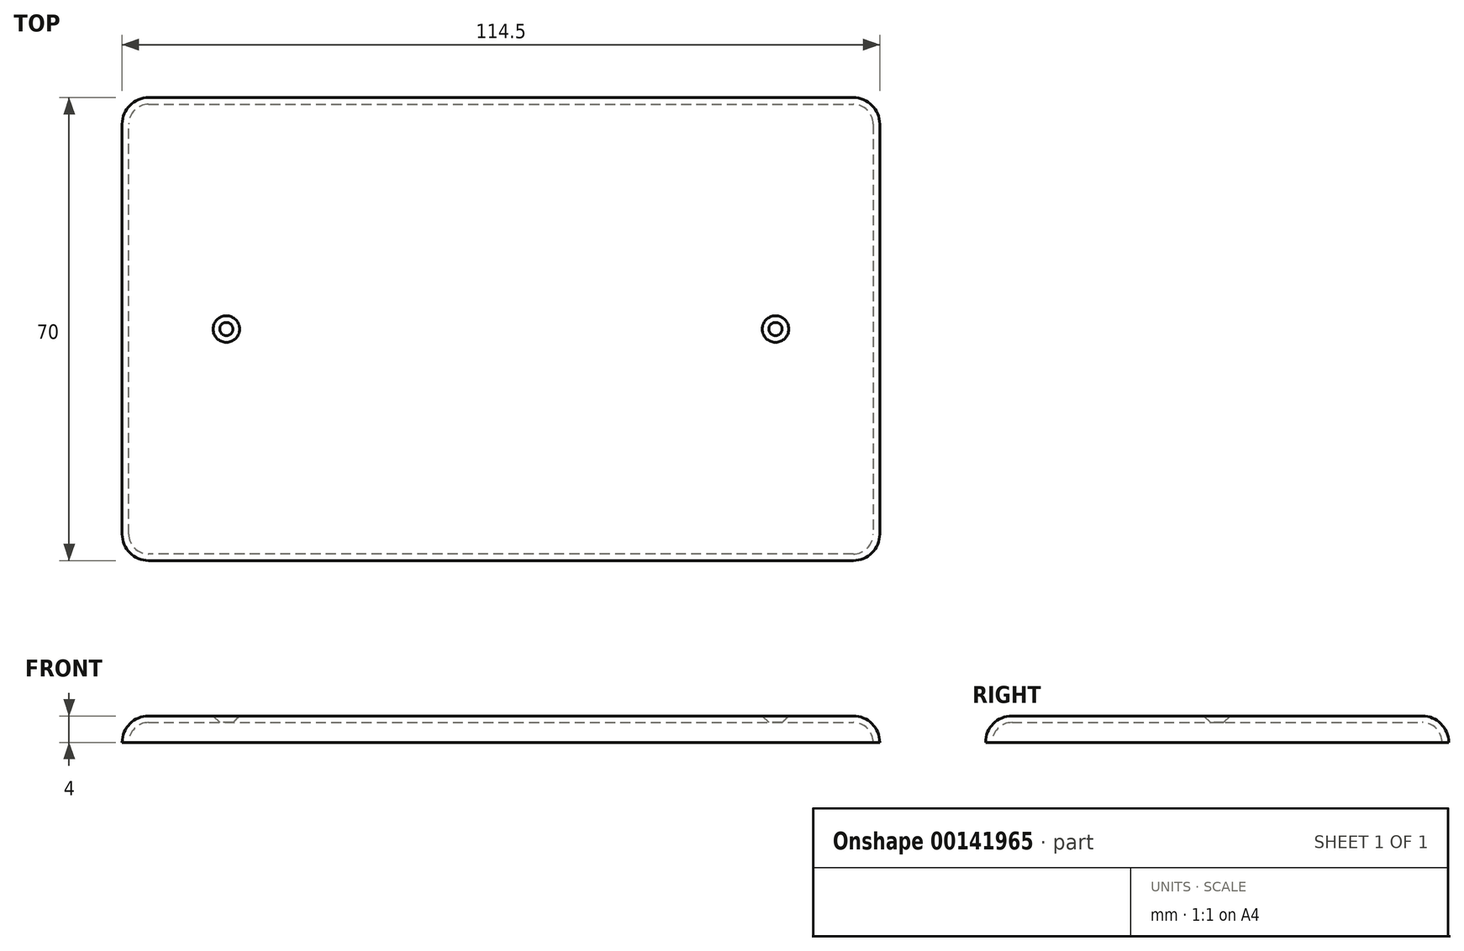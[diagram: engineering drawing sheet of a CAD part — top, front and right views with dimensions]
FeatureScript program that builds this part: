
annotation { "Feature Type Name" : "Feature", "Feature Type Description" : "" }
export const myFeature = defineFeature(function(context is Context, id is Id, definition is map)
    precondition{}
    {
        {
            var Q0;
            Q0=qCreatedBy(makeId("Top.planeOp"),FACE);
            var sketch = newSketch(context, id + "F0", { "sketchPlane" : qUnion([Q0])});
            skLineSegment(sketch, "E0.bottom", {"start": v(-57.25, 35) * mm, "end": v(57.25, 35) * mm});
            skLineSegment(sketch, "E0.top", {"start": v(-57.25, -35) * mm, "end": v(57.25, -35) * mm});
            skLineSegment(sketch, "E0.left", {"start": v(-57.25, 35) * mm, "end": v(-57.25, -35) * mm});
            skLineSegment(sketch, "E0.right", {"start": v(57.25, 35) * mm, "end": v(57.25, -35) * mm});
            skSolve(sketch);
        }
        {
            var Q0;
            Q0=makeQuery(id+"F0.imprint","IMPRINT",FACE,{"disambiguationData":[TD([[makeQuery(id+"F0.imprint","IMPRINT",EDGE,{"derivedFrom":sQuery(id+"F0.wireOp",EDGE,"E0.bottom")}),-1.0]])]});
            extrude(context, id + "F1", {"entities" : qUnion([Q0]), "depth" : 4 * mm});
        }
        {
            var Q0;
            Q0=makeQuery(id+"F1.opExtrude","CAP_EDGE",EDGE,{"disambiguationData":[OSD([sQuery(id+"F0.wireOp",EDGE,"E0.left")])],"isStart":false});
            var Q1;
            Q1=makeQuery(id+"F1.opExtrude","CAP_EDGE",EDGE,{"disambiguationData":[OSD([sQuery(id+"F0.wireOp",EDGE,"E0.bottom")])],"isStart":false});
            var Q2;
            Q2=makeQuery(id+"F1.opExtrude","CAP_EDGE",EDGE,{"disambiguationData":[OSD([sQuery(id+"F0.wireOp",EDGE,"E0.top")])],"isStart":false});
            var Q3;
            Q3=makeQuery(id+"F1.opExtrude","SWEPT_EDGE",EDGE,{"disambiguationData":[OSD([sQuery(id+"F0.wireOp",EDGE,"E0.top"),sQuery(id+"F0.wireOp",EDGE,"E0.left")])]});
            var Q4;
            Q4=makeQuery(id+"F1.opExtrude","SWEPT_EDGE",EDGE,{"disambiguationData":[OSD([sQuery(id+"F0.wireOp",EDGE,"E0.bottom"),sQuery(id+"F0.wireOp",EDGE,"E0.left")])]});
            var Q5;
            Q5=makeQuery(id+"F1.opExtrude","SWEPT_EDGE",EDGE,{"disambiguationData":[OSD([sQuery(id+"F0.wireOp",EDGE,"E0.bottom"),sQuery(id+"F0.wireOp",EDGE,"E0.right")])]});
            var Q6;
            Q6=makeQuery(id+"F1.opExtrude","CAP_EDGE",EDGE,{"disambiguationData":[OSD([sQuery(id+"F0.wireOp",EDGE,"E0.right")])],"isStart":false});
            var Q7;
            Q7=makeQuery(id+"F1.opExtrude","SWEPT_EDGE",EDGE,{"disambiguationData":[OSD([sQuery(id+"F0.wireOp",EDGE,"E0.top"),sQuery(id+"F0.wireOp",EDGE,"E0.right")])]});
            fillet(context, id + "F2", {"entities" : qUnion([Q0, Q1, Q2, Q3, Q4, Q5, Q6, Q7]), "radius" : 4 * mm, "allowEdgeOverflow" : false});
        }
        {
            var Q0;
            Q0=makeQuery(id+"F1.opExtrude","CAP_FACE",FACE,{"disambiguationData":[OSD([sQuery(id+"F0.wireOp",EDGE,"E0.bottom"),sQuery(id+"F0.wireOp",EDGE,"E0.top"),sQuery(id+"F0.wireOp",EDGE,"E0.left"),sQuery(id+"F0.wireOp",EDGE,"E0.right")])],"isStart":true});
            shell(context, id + "F3", {"entities" : qUnion([Q0]), "thickness" : 1 * mm});
        }
        {
            var Q0;
            Q0=makeQuery(id+"F1.opExtrude","CAP_FACE",FACE,{"disambiguationData":[OSD([sQuery(id+"F0.wireOp",EDGE,"E0.bottom"),sQuery(id+"F0.wireOp",EDGE,"E0.top"),sQuery(id+"F0.wireOp",EDGE,"E0.left"),sQuery(id+"F0.wireOp",EDGE,"E0.right")])],"isStart":false});
            var sketch = newSketch(context, id + "F4", { "sketchPlane" : qUnion([Q0])});
            skLineSegment(sketch, "E1", {"start": v(53.25, 0) * mm, "end": v(-53.25, 0) * mm, "construction": true});
            skPoint(sketch, "E2", {"position": v(41.5, 0) * mm});
            skPoint(sketch, "E3", {"position": v(-41.5, 0) * mm});
            skSolve(sketch);
        }
        {
            var Q0;
            Q0=sQuery(id+"F4.wireOp",VERTEX,"E2");
            var Q1;
            Q1=sQuery(id+"F4.wireOp",VERTEX,"E3");
            var Q2;
            Q2=makeQuery(id+"F1.opExtrude","SWEPT_BODY",BODY,{"disambiguationData":[OSD([sQuery(id+"F0.wireOp",EDGE,"E0.bottom"),sQuery(id+"F0.wireOp",EDGE,"E0.top"),sQuery(id+"F0.wireOp",EDGE,"E0.left"),sQuery(id+"F0.wireOp",EDGE,"E0.right")])]});
            hole(context, id + "F5", {"style" : HoleStyle.C_SINK, "endStyle" : HoleEndStyle.THROUGH, "holeDiameter" : 2 * mm, "cSinkDiameter" : 4 * mm, "cSinkAngle" : 90 * degree, "startFromSketch" : true, "locations" : qUnion([Q0, Q1]), "scope" : qUnion([Q2]), "isTappedThrough" : true});
        }
    });
